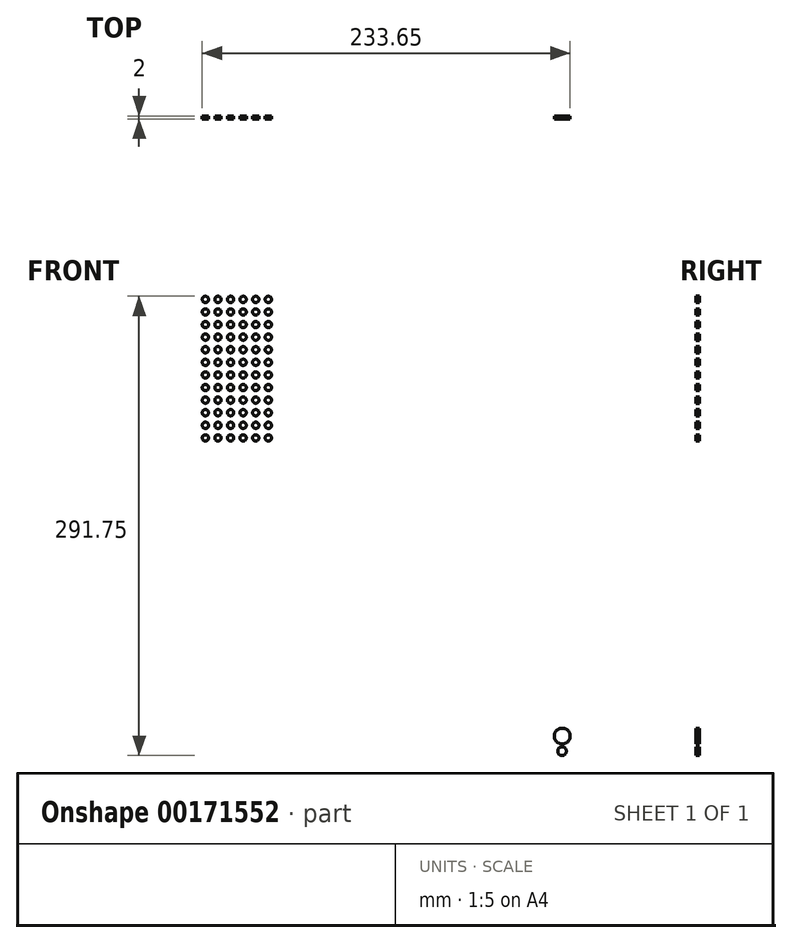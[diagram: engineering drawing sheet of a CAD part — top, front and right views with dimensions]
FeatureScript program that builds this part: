
annotation { "Feature Type Name" : "Feature", "Feature Type Description" : "" }
export const myFeature = defineFeature(function(context is Context, id is Id, definition is map)
    precondition{}
    {
        {
            var Q0;
            Q0=qCreatedBy(makeId("Front.planeOp"),FACE);
            var sketch = newSketch(context, id + "F0", { "sketchPlane" : qUnion([Q0])});
            skPoint(sketch, "E0.middle", {"position": v(0, 0) * mm});
            skLineSegment(sketch, "E1.bottom", {"start": v(127.48, 155) * mm, "end": v(157.77, 155) * mm});
            skLineSegment(sketch, "E1.top", {"start": v(127.48, -155) * mm, "end": v(158.23, -155) * mm});
            skLineSegment(sketch, "E1.right", {"start": v(157.77, 155) * mm, "end": v(158.23, -155) * mm});
            skLineSegment(sketch, "E2.bottom", {"start": v(-127.94, 155) * mm, "end": v(-158.23, 155) * mm});
            skLineSegment(sketch, "E2.top", {"start": v(-127.02, -155) * mm, "end": v(-157.77, -155) * mm});
            skLineSegment(sketch, "E2.right", {"start": v(-158.23, 155) * mm, "end": v(-157.77, -155) * mm});
            skLineSegment(sketch, "E3.top", {"start": v(-125.23, 188.22) * mm, "end": v(124.77, 188.22) * mm});
            skLineSegment(sketch, "E3.left", {"start": v(-125.23, 157.7) * mm, "end": v(-125.23, 188.22) * mm});
            skLineSegment(sketch, "E3.right", {"start": v(124.77, 157.7) * mm, "end": v(124.77, 188.22) * mm});
            skLineSegment(sketch, "E4.top", {"start": v(-124.77, -187.78) * mm, "end": v(124.77, -187.78) * mm});
            skLineSegment(sketch, "E4.left", {"start": v(-124.77, -157.26) * mm, "end": v(-124.77, -187.78) * mm});
            skLineSegment(sketch, "E4.right", {"start": v(124.77, -157.26) * mm, "end": v(124.77, -187.78) * mm});
            skLineSegment(sketch, "E5.bottom", {"start": v(-122.53, 157.7) * mm, "end": v(-125.23, 157.7) * mm});
            skLineSegment(sketch, "E5.top", {"start": v(-122.53, 152.3) * mm, "end": v(-127.94, 152.3) * mm});
            skLineSegment(sketch, "E5.left", {"start": v(-122.53, 157.7) * mm, "end": v(-122.53, 152.3) * mm});
            skLineSegment(sketch, "E5.right", {"start": v(-127.94, 155) * mm, "end": v(-127.94, 152.3) * mm});
            skPoint(sketch, "E5.middle", {"position": v(-125.23, 155) * mm});
            skLineSegment(sketch, "E6.bottom", {"start": v(124.77, 157.7) * mm, "end": v(122.06, 157.7) * mm});
            skLineSegment(sketch, "E6.top", {"start": v(127.48, 152.32) * mm, "end": v(122.06, 152.32) * mm});
            skLineSegment(sketch, "E6.left", {"start": v(127.48, 155) * mm, "end": v(127.48, 152.32) * mm});
            skLineSegment(sketch, "E6.right", {"start": v(122.06, 157.7) * mm, "end": v(122.06, 152.32) * mm});
            skPoint(sketch, "E6.middle", {"position": v(124.77, 155) * mm});
            skLineSegment(sketch, "E7.bottom", {"start": v(127.48, -152.73) * mm, "end": v(122.98, -152.73) * mm});
            skLineSegment(sketch, "E7.top", {"start": v(124.77, -157.26) * mm, "end": v(122.98, -157.26) * mm});
            skLineSegment(sketch, "E7.left", {"start": v(127.48, -152.73) * mm, "end": v(127.48, -155) * mm});
            skLineSegment(sketch, "E7.right", {"start": v(122.98, -152.73) * mm, "end": v(122.98, -157.26) * mm});
            skPoint(sketch, "E7.middle", {"position": v(125.23, -155) * mm});
            skLineSegment(sketch, "E8.bottom", {"start": v(-122.52, -152.76) * mm, "end": v(-127.02, -152.76) * mm});
            skLineSegment(sketch, "E8.top", {"start": v(-122.52, -157.26) * mm, "end": v(-124.77, -157.26) * mm});
            skLineSegment(sketch, "E8.left", {"start": v(-122.52, -152.76) * mm, "end": v(-122.52, -157.26) * mm});
            skLineSegment(sketch, "E8.right", {"start": v(-127.02, -152.76) * mm, "end": v(-127.02, -155) * mm});
            skPoint(sketch, "E8.middle", {"position": v(-124.77, -155) * mm});
            skPoint(sketch, "E9.orphan", {"position": v(127.48, 157.7) * mm});
            skPoint(sketch, "E10.orphan", {"position": v(127.48, -157.26) * mm});
            skPoint(sketch, "E11.orphan", {"position": v(-127.02, -157.26) * mm});
            skLineSegment(sketch, "E12", {"start": v(-133.23, 167.46) * mm, "end": v(-132.73, -167.53) * mm, "construction": true});
            skLineSegment(sketch, "E13.bottom", {"start": v(55, 130.25) * mm, "end": v(-55, 130.25) * mm});
            skLineSegment(sketch, "E13.top", {"start": v(55, 59.75) * mm, "end": v(-55, 59.75) * mm});
            skLineSegment(sketch, "E13.left", {"start": v(55, 130.25) * mm, "end": v(55, 59.75) * mm});
            skLineSegment(sketch, "E13.right", {"start": v(-55, 130.25) * mm, "end": v(-55, 59.75) * mm});
            skPoint(sketch, "E13.middle", {"position": v(0, 95) * mm});
            skLineSegment(sketch, "E14.bottom", {"start": v(59, 134.5) * mm, "end": v(-59, 134.5) * mm, "construction": true});
            skLineSegment(sketch, "E14.top", {"start": v(59, 55.5) * mm, "end": v(-59, 55.5) * mm, "construction": true});
            skLineSegment(sketch, "E14.left", {"start": v(59, 134.5) * mm, "end": v(59, 55.5) * mm, "construction": true});
            skLineSegment(sketch, "E14.right", {"start": v(-59, 134.5) * mm, "end": v(-59, 55.5) * mm, "construction": true});
            skCircle(sketch, "E15", {"center": v(-59, 134.5) * mm, "radius": 2.75 * mm});
            skCircle(sketch, "E16", {"center": v(-59, 55.5) * mm, "radius": 2.75 * mm});
            skCircle(sketch, "E17", {"center": v(59, 55.5) * mm, "radius": 2.75 * mm});
            skCircle(sketch, "E18", {"center": v(59, 134.5) * mm, "radius": 2.75 * mm});
            skLineSegment(sketch, "E19.bottom", {"start": v(65, 140.5) * mm, "end": v(-65, 140.5) * mm, "construction": true});
            skLineSegment(sketch, "E19.top", {"start": v(65, 49.5) * mm, "end": v(-65, 49.5) * mm, "construction": true});
            skLineSegment(sketch, "E19.left", {"start": v(65, 140.5) * mm, "end": v(65, 49.5) * mm, "construction": true});
            skLineSegment(sketch, "E19.right", {"start": v(-65, 140.5) * mm, "end": v(-65, 49.5) * mm, "construction": true});
            skCircle(sketch, "E20", {"center": v(-150.33, -112.4) * mm, "radius": 4 * mm});
            skCircle(sketch, "E21", {"center": v(-150.33, 34.3) * mm, "radius": 4.5 * mm});
            skCircle(sketch, "E22", {"center": v(-150.33, 149.07) * mm, "radius": 4.5 * mm});
            skCircle(sketch, "E23", {"center": v(-150.33, 72.92) * mm, "radius": 4.5 * mm});
            skCircle(sketch, "E24.MirrorC", {"center": v(150.33, 149.07) * mm, "radius": 4.5 * mm});
            skCircle(sketch, "E25.MirrorC", {"center": v(150.33, 72.92) * mm, "radius": 4.5 * mm});
            skCircle(sketch, "E26.MirrorC", {"center": v(150.33, 34.3) * mm, "radius": 4.5 * mm});
            skCircle(sketch, "E27.MirrorC", {"center": v(150.33, -112.4) * mm, "radius": 4 * mm});
            skCircle(sketch, "E28", {"center": v(0, -175.28) * mm, "radius": 4 * mm});
            skCircle(sketch, "E29", {"center": v(-95, -175.28) * mm, "radius": 4 * mm});
            skCircle(sketch, "E30", {"center": v(95, -175.28) * mm, "radius": 4 * mm});
            skCircle(sketch, "E31.MirrorC", {"center": v(-95, 175.28) * mm, "radius": 4 * mm});
            skCircle(sketch, "E32.MirrorC", {"center": v(95, 175.28) * mm, "radius": 4 * mm});
            skCircle(sketch, "E33.MirrorC", {"center": v(0, 175.28) * mm, "radius": 4 * mm});
            skSolve(sketch);
        }
        {
            var Q0;
            Q0=makeQuery(id+"F0.imprint","IMPRINT",FACE,{"disambiguationData":[TD([[makeQuery(id+"F0.imprint","IMPRINT",EDGE,{"derivedFrom":sQuery(id+"F0.wireOp",EDGE,"E1.bottom")}),-1.0]])]});
            extrude(context, id + "F1", {"entities" : qUnion([Q0]), "endBound" : BoundingType.SYMMETRIC, "depth" : 2 * mm});
        }
        {
            var Q0;
            Q0=makeQuery(id+"F1.opExtrude","SWEPT_EDGE",EDGE,{"disambiguationData":[OSD([sQuery(id+"F0.wireOp",EDGE,"E1.bottom"),sQuery(id+"F0.wireOp",EDGE,"E1.right")])]});
            var Q1;
            Q1=makeQuery(id+"F1.opExtrude","SWEPT_EDGE",EDGE,{"disambiguationData":[OSD([sQuery(id+"F0.wireOp",EDGE,"E3.top"),sQuery(id+"F0.wireOp",EDGE,"E3.right")])]});
            var Q2;
            Q2=makeQuery(id+"F1.opExtrude","SWEPT_EDGE",EDGE,{"disambiguationData":[OSD([sQuery(id+"F0.wireOp",EDGE,"E3.top"),sQuery(id+"F0.wireOp",EDGE,"E3.left")])]});
            var Q3;
            Q3=makeQuery(id+"F1.opExtrude","SWEPT_EDGE",EDGE,{"disambiguationData":[OSD([sQuery(id+"F0.wireOp",EDGE,"E2.bottom"),sQuery(id+"F0.wireOp",EDGE,"E2.right")])]});
            var Q4;
            Q4=makeQuery(id+"F1.opExtrude","SWEPT_EDGE",EDGE,{"disambiguationData":[OSD([sQuery(id+"F0.wireOp",EDGE,"E1.top"),sQuery(id+"F0.wireOp",EDGE,"E1.right")])]});
            var Q5;
            Q5=makeQuery(id+"F1.opExtrude","SWEPT_EDGE",EDGE,{"disambiguationData":[OSD([sQuery(id+"F0.wireOp",EDGE,"E4.top"),sQuery(id+"F0.wireOp",EDGE,"E4.right")])]});
            var Q6;
            Q6=makeQuery(id+"F1.opExtrude","SWEPT_EDGE",EDGE,{"disambiguationData":[OSD([sQuery(id+"F0.wireOp",EDGE,"E4.top"),sQuery(id+"F0.wireOp",EDGE,"E4.left")])]});
            var Q7;
            Q7=makeQuery(id+"F1.opExtrude","SWEPT_EDGE",EDGE,{"disambiguationData":[OSD([sQuery(id+"F0.wireOp",EDGE,"E2.top"),sQuery(id+"F0.wireOp",EDGE,"E2.right")])]});
            chamfer(context, id + "F2", {"entities" : qUnion([Q0, Q1, Q2, Q3, Q4, Q5, Q6, Q7]), "width" : 6 * mm, "tangentPropagation" : true});
        }
        {
            var Q0;
            Q0=makeQuery(id+"F1.opExtrude","CAP_FACE",FACE,{"disambiguationData":[OSD([sQuery(id+"F0.wireOp",EDGE,"E1.bottom"),sQuery(id+"F0.wireOp",EDGE,"E1.top"),sQuery(id+"F0.wireOp",EDGE,"E1.right"),sQuery(id+"F0.wireOp",EDGE,"E2.bottom"),sQuery(id+"F0.wireOp",EDGE,"E2.top"),sQuery(id+"F0.wireOp",EDGE,"E2.right"),sQuery(id+"F0.wireOp",EDGE,"E3.top"),sQuery(id+"F0.wireOp",EDGE,"E3.left"),sQuery(id+"F0.wireOp",EDGE,"E3.right"),sQuery(id+"F0.wireOp",EDGE,"E4.top"),sQuery(id+"F0.wireOp",EDGE,"E4.left"),sQuery(id+"F0.wireOp",EDGE,"E4.right"),sQuery(id+"F0.wireOp",EDGE,"E5.bottom"),sQuery(id+"F0.wireOp",EDGE,"E5.top"),sQuery(id+"F0.wireOp",EDGE,"E5.left"),sQuery(id+"F0.wireOp",EDGE,"E5.right"),sQuery(id+"F0.wireOp",EDGE,"E6.bottom"),sQuery(id+"F0.wireOp",EDGE,"E6.top"),sQuery(id+"F0.wireOp",EDGE,"E6.left"),sQuery(id+"F0.wireOp",EDGE,"E6.right"),sQuery(id+"F0.wireOp",EDGE,"E7.bottom"),sQuery(id+"F0.wireOp",EDGE,"E7.top"),sQuery(id+"F0.wireOp",EDGE,"E7.left"),sQuery(id+"F0.wireOp",EDGE,"E7.right"),sQuery(id+"F0.wireOp",EDGE,"E8.bottom"),sQuery(id+"F0.wireOp",EDGE,"E8.top"),sQuery(id+"F0.wireOp",EDGE,"E8.left"),sQuery(id+"F0.wireOp",EDGE,"E8.right"),sQuery(id+"F0.wireOp",EDGE,"E13.bottom"),sQuery(id+"F0.wireOp",EDGE,"E13.top"),sQuery(id+"F0.wireOp",EDGE,"E13.left"),sQuery(id+"F0.wireOp",EDGE,"E13.right"),sQuery(id+"F0.wireOp",EDGE,"E15"),sQuery(id+"F0.wireOp",EDGE,"E16"),sQuery(id+"F0.wireOp",EDGE,"E17"),sQuery(id+"F0.wireOp",EDGE,"E18")])],"isStart":false});
            var sketch = newSketch(context, id + "F3", { "sketchPlane" : qUnion([Q0])});
            skCircle(sketch, "E34", {"center": v(109.77, -140) * mm, "radius": 2.75 * mm});
            skLineSegment(sketch, "E35", {"start": v(106.88, -130.39) * mm, "end": v(112.88, -130.39) * mm});
            skLineSegment(sketch, "E36", {"start": v(107.88, -131.39) * mm, "end": v(111.88, -131.39) * mm});
            skLineSegment(sketch, "E37", {"start": v(108.88, -132.39) * mm, "end": v(110.88, -132.39) * mm});
            skLineSegment(sketch, "E38", {"start": v(109.88, -130.39) * mm, "end": v(109.88, -126.39) * mm});
            skCircle(sketch, "E39", {"center": v(109.88, -130.39) * mm, "radius": 5 * mm});
            skSolve(sketch);
        }
        {
            var Q0;
            Q0=makeQuery(id+"F3.imprint","IMPRINT",FACE,{"disambiguationData":[TD([[makeQuery(id+"F3.imprint","IMPRINT",EDGE,{"derivedFrom":sQuery(id+"F3.wireOp",EDGE,"E34")}),-1.0]])]});
            var sketch = newSketch(context, id + "F4", { "sketchPlane" : qUnion([Q0])});
            skCircle(sketch, "E40", {"center": v(116.77, 147) * mm, "radius": 2 * mm});
            skCircle(sketch, "E41.0.1.0", {"center": v(116.77, 139) * mm, "radius": 2 * mm});
            skCircle(sketch, "E41.0.2.0", {"center": v(116.77, 131) * mm, "radius": 2 * mm});
            skCircle(sketch, "E41.0.3.0", {"center": v(116.77, 123) * mm, "radius": 2 * mm});
            skCircle(sketch, "E41.0.4.0", {"center": v(116.77, 115) * mm, "radius": 2 * mm});
            skCircle(sketch, "E41.0.5.0", {"center": v(116.77, 107) * mm, "radius": 2 * mm});
            skCircle(sketch, "E41.0.6.0", {"center": v(116.77, 99) * mm, "radius": 2 * mm});
            skCircle(sketch, "E41.0.7.0", {"center": v(116.77, 91) * mm, "radius": 2 * mm});
            skCircle(sketch, "E41.0.8.0", {"center": v(116.77, 83) * mm, "radius": 2 * mm});
            skCircle(sketch, "E41.0.9.0", {"center": v(116.77, 75) * mm, "radius": 2 * mm});
            skCircle(sketch, "E41.0.10.0", {"center": v(116.77, 67) * mm, "radius": 2 * mm});
            skCircle(sketch, "E41.0.11.0", {"center": v(116.77, 59) * mm, "radius": 2 * mm});
            skCircle(sketch, "E41.1.0.0", {"center": v(108.77, 147) * mm, "radius": 2 * mm});
            skCircle(sketch, "E41.1.1.0", {"center": v(108.77, 139) * mm, "radius": 2 * mm});
            skCircle(sketch, "E41.1.2.0", {"center": v(108.77, 131) * mm, "radius": 2 * mm});
            skCircle(sketch, "E41.1.3.0", {"center": v(108.77, 123) * mm, "radius": 2 * mm});
            skCircle(sketch, "E41.1.4.0", {"center": v(108.77, 115) * mm, "radius": 2 * mm});
            skCircle(sketch, "E41.1.5.0", {"center": v(108.77, 107) * mm, "radius": 2 * mm});
            skCircle(sketch, "E41.1.6.0", {"center": v(108.77, 99) * mm, "radius": 2 * mm});
            skCircle(sketch, "E41.1.7.0", {"center": v(108.77, 91) * mm, "radius": 2 * mm});
            skCircle(sketch, "E41.1.8.0", {"center": v(108.77, 83) * mm, "radius": 2 * mm});
            skCircle(sketch, "E41.1.9.0", {"center": v(108.77, 75) * mm, "radius": 2 * mm});
            skCircle(sketch, "E41.1.10.0", {"center": v(108.77, 67) * mm, "radius": 2 * mm});
            skCircle(sketch, "E41.1.11.0", {"center": v(108.77, 59) * mm, "radius": 2 * mm});
            skCircle(sketch, "E41.2.0.0", {"center": v(100.77, 147) * mm, "radius": 2 * mm});
            skCircle(sketch, "E41.2.1.0", {"center": v(100.77, 139) * mm, "radius": 2 * mm});
            skCircle(sketch, "E41.2.2.0", {"center": v(100.77, 131) * mm, "radius": 2 * mm});
            skCircle(sketch, "E41.2.3.0", {"center": v(100.77, 123) * mm, "radius": 2 * mm});
            skCircle(sketch, "E41.2.4.0", {"center": v(100.77, 115) * mm, "radius": 2 * mm});
            skCircle(sketch, "E41.2.5.0", {"center": v(100.77, 107) * mm, "radius": 2 * mm});
            skCircle(sketch, "E41.2.6.0", {"center": v(100.77, 99) * mm, "radius": 2 * mm});
            skCircle(sketch, "E41.2.7.0", {"center": v(100.77, 91) * mm, "radius": 2 * mm});
            skCircle(sketch, "E41.2.8.0", {"center": v(100.77, 83) * mm, "radius": 2 * mm});
            skCircle(sketch, "E41.2.9.0", {"center": v(100.77, 75) * mm, "radius": 2 * mm});
            skCircle(sketch, "E41.2.10.0", {"center": v(100.77, 67) * mm, "radius": 2 * mm});
            skCircle(sketch, "E41.2.11.0", {"center": v(100.77, 59) * mm, "radius": 2 * mm});
            skCircle(sketch, "E41.3.0.0", {"center": v(92.77, 147) * mm, "radius": 2 * mm});
            skCircle(sketch, "E41.3.1.0", {"center": v(92.77, 139) * mm, "radius": 2 * mm});
            skCircle(sketch, "E41.3.2.0", {"center": v(92.77, 131) * mm, "radius": 2 * mm});
            skCircle(sketch, "E41.3.3.0", {"center": v(92.77, 123) * mm, "radius": 2 * mm});
            skCircle(sketch, "E41.3.4.0", {"center": v(92.77, 115) * mm, "radius": 2 * mm});
            skCircle(sketch, "E41.3.5.0", {"center": v(92.77, 107) * mm, "radius": 2 * mm});
            skCircle(sketch, "E41.3.6.0", {"center": v(92.77, 99) * mm, "radius": 2 * mm});
            skCircle(sketch, "E41.3.7.0", {"center": v(92.77, 91) * mm, "radius": 2 * mm});
            skCircle(sketch, "E41.3.8.0", {"center": v(92.77, 83) * mm, "radius": 2 * mm});
            skCircle(sketch, "E41.3.9.0", {"center": v(92.77, 75) * mm, "radius": 2 * mm});
            skCircle(sketch, "E41.3.10.0", {"center": v(92.77, 67) * mm, "radius": 2 * mm});
            skCircle(sketch, "E41.3.11.0", {"center": v(92.77, 59) * mm, "radius": 2 * mm});
            skCircle(sketch, "E41.4.0.0", {"center": v(84.77, 147) * mm, "radius": 2 * mm});
            skCircle(sketch, "E41.4.1.0", {"center": v(84.77, 139) * mm, "radius": 2 * mm});
            skCircle(sketch, "E41.4.2.0", {"center": v(84.77, 131) * mm, "radius": 2 * mm});
            skCircle(sketch, "E41.4.3.0", {"center": v(84.77, 123) * mm, "radius": 2 * mm});
            skCircle(sketch, "E41.4.4.0", {"center": v(84.77, 115) * mm, "radius": 2 * mm});
            skCircle(sketch, "E41.4.5.0", {"center": v(84.77, 107) * mm, "radius": 2 * mm});
            skCircle(sketch, "E41.4.6.0", {"center": v(84.77, 99) * mm, "radius": 2 * mm});
            skCircle(sketch, "E41.4.7.0", {"center": v(84.77, 91) * mm, "radius": 2 * mm});
            skCircle(sketch, "E41.4.8.0", {"center": v(84.77, 83) * mm, "radius": 2 * mm});
            skCircle(sketch, "E41.4.9.0", {"center": v(84.77, 75) * mm, "radius": 2 * mm});
            skCircle(sketch, "E41.4.10.0", {"center": v(84.77, 67) * mm, "radius": 2 * mm});
            skCircle(sketch, "E41.4.11.0", {"center": v(84.77, 59) * mm, "radius": 2 * mm});
            skCircle(sketch, "E41.5.0.0", {"center": v(76.77, 147) * mm, "radius": 2 * mm});
            skCircle(sketch, "E41.5.1.0", {"center": v(76.77, 139) * mm, "radius": 2 * mm});
            skCircle(sketch, "E41.5.2.0", {"center": v(76.77, 131) * mm, "radius": 2 * mm});
            skCircle(sketch, "E41.5.3.0", {"center": v(76.77, 123) * mm, "radius": 2 * mm});
            skCircle(sketch, "E41.5.4.0", {"center": v(76.77, 115) * mm, "radius": 2 * mm});
            skCircle(sketch, "E41.5.5.0", {"center": v(76.77, 107) * mm, "radius": 2 * mm});
            skCircle(sketch, "E41.5.6.0", {"center": v(76.77, 99) * mm, "radius": 2 * mm});
            skCircle(sketch, "E41.5.7.0", {"center": v(76.77, 91) * mm, "radius": 2 * mm});
            skCircle(sketch, "E41.5.8.0", {"center": v(76.77, 83) * mm, "radius": 2 * mm});
            skCircle(sketch, "E41.5.9.0", {"center": v(76.77, 75) * mm, "radius": 2 * mm});
            skCircle(sketch, "E41.5.10.0", {"center": v(76.77, 67) * mm, "radius": 2 * mm});
            skCircle(sketch, "E41.5.11.0", {"center": v(76.77, 59) * mm, "radius": 2 * mm});
            skLineSegment(sketch, "E41.direction1", {"start": v(116.77, 147) * mm, "end": v(108.77, 147) * mm, "construction": true});
            skLineSegment(sketch, "E41.direction2", {"start": v(116.77, 147) * mm, "end": v(116.77, 139) * mm, "construction": true});
            skCircle(sketch, "E42.MirrorC", {"center": v(-116.77, 147) * mm, "radius": 2 * mm});
            skCircle(sketch, "E43.MirrorC", {"center": v(-108.77, 147) * mm, "radius": 2 * mm});
            skCircle(sketch, "E44.MirrorC", {"center": v(-116.77, 139) * mm, "radius": 2 * mm});
            skCircle(sketch, "E45.MirrorC", {"center": v(-76.77, 75) * mm, "radius": 2 * mm});
            skCircle(sketch, "E46.MirrorC", {"center": v(-76.77, 131) * mm, "radius": 2 * mm});
            skCircle(sketch, "E47.MirrorC", {"center": v(-108.77, 75) * mm, "radius": 2 * mm});
            skCircle(sketch, "E48.MirrorC", {"center": v(-92.77, 139) * mm, "radius": 2 * mm});
            skCircle(sketch, "E49.MirrorC", {"center": v(-100.77, 99) * mm, "radius": 2 * mm});
            skCircle(sketch, "E50.MirrorC", {"center": v(-92.77, 67) * mm, "radius": 2 * mm});
            skCircle(sketch, "E51.MirrorC", {"center": v(-84.77, 107) * mm, "radius": 2 * mm});
            skCircle(sketch, "E52.MirrorC", {"center": v(-92.77, 83) * mm, "radius": 2 * mm});
            skCircle(sketch, "E53.MirrorC", {"center": v(-76.77, 147) * mm, "radius": 2 * mm});
            skCircle(sketch, "E54.MirrorC", {"center": v(-100.77, 115) * mm, "radius": 2 * mm});
            skCircle(sketch, "E55.MirrorC", {"center": v(-76.77, 83) * mm, "radius": 2 * mm});
            skCircle(sketch, "E56.MirrorC", {"center": v(-76.77, 139) * mm, "radius": 2 * mm});
            skCircle(sketch, "E57.MirrorC", {"center": v(-116.77, 59) * mm, "radius": 2 * mm});
            skCircle(sketch, "E58.MirrorC", {"center": v(-108.77, 83) * mm, "radius": 2 * mm});
            skCircle(sketch, "E59.MirrorC", {"center": v(-92.77, 147) * mm, "radius": 2 * mm});
            skCircle(sketch, "E60.MirrorC", {"center": v(-100.77, 107) * mm, "radius": 2 * mm});
            skCircle(sketch, "E61.MirrorC", {"center": v(-92.77, 75) * mm, "radius": 2 * mm});
            skCircle(sketch, "E62.MirrorC", {"center": v(-84.77, 115) * mm, "radius": 2 * mm});
            skCircle(sketch, "E63.MirrorC", {"center": v(-116.77, 67) * mm, "radius": 2 * mm});
            skCircle(sketch, "E64.MirrorC", {"center": v(-116.77, 75) * mm, "radius": 2 * mm});
            skCircle(sketch, "E65.MirrorC", {"center": v(-116.77, 83) * mm, "radius": 2 * mm});
            skCircle(sketch, "E66.MirrorC", {"center": v(-116.77, 91) * mm, "radius": 2 * mm});
            skCircle(sketch, "E67.MirrorC", {"center": v(-116.77, 99) * mm, "radius": 2 * mm});
            skCircle(sketch, "E68.MirrorC", {"center": v(-116.77, 107) * mm, "radius": 2 * mm});
            skCircle(sketch, "E69.MirrorC", {"center": v(-92.77, 91) * mm, "radius": 2 * mm});
            skCircle(sketch, "E70.MirrorC", {"center": v(-84.77, 59) * mm, "radius": 2 * mm});
            skCircle(sketch, "E71.MirrorC", {"center": v(-116.77, 115) * mm, "radius": 2 * mm});
            skCircle(sketch, "E72.MirrorC", {"center": v(-116.77, 123) * mm, "radius": 2 * mm});
            skCircle(sketch, "E73.MirrorC", {"center": v(-100.77, 123) * mm, "radius": 2 * mm});
            skCircle(sketch, "E74.MirrorC", {"center": v(-116.77, 131) * mm, "radius": 2 * mm});
            skCircle(sketch, "E75.MirrorC", {"center": v(-108.77, 123) * mm, "radius": 2 * mm});
            skCircle(sketch, "E76.MirrorC", {"center": v(-108.77, 131) * mm, "radius": 2 * mm});
            skCircle(sketch, "E77.MirrorC", {"center": v(-108.77, 139) * mm, "radius": 2 * mm});
            skCircle(sketch, "E78.MirrorC", {"center": v(-76.77, 91) * mm, "radius": 2 * mm});
            skCircle(sketch, "E79.MirrorC", {"center": v(-108.77, 91) * mm, "radius": 2 * mm});
            skCircle(sketch, "E80.MirrorC", {"center": v(-100.77, 59) * mm, "radius": 2 * mm});
            skCircle(sketch, "E81.MirrorC", {"center": v(-84.77, 123) * mm, "radius": 2 * mm});
            skCircle(sketch, "E82.MirrorC", {"center": v(-92.77, 99) * mm, "radius": 2 * mm});
            skCircle(sketch, "E83.MirrorC", {"center": v(-84.77, 67) * mm, "radius": 2 * mm});
            skCircle(sketch, "E84.MirrorC", {"center": v(-100.77, 131) * mm, "radius": 2 * mm});
            skCircle(sketch, "E85.MirrorC", {"center": v(-76.77, 99) * mm, "radius": 2 * mm});
            skCircle(sketch, "E86.MirrorC", {"center": v(-108.77, 99) * mm, "radius": 2 * mm});
            skCircle(sketch, "E87.MirrorC", {"center": v(-100.77, 67) * mm, "radius": 2 * mm});
            skCircle(sketch, "E88.MirrorC", {"center": v(-84.77, 131) * mm, "radius": 2 * mm});
            skCircle(sketch, "E89.MirrorC", {"center": v(-92.77, 107) * mm, "radius": 2 * mm});
            skCircle(sketch, "E90.MirrorC", {"center": v(-84.77, 75) * mm, "radius": 2 * mm});
            skLineSegment(sketch, "E91.MirrorCS", {"start": v(-116.77, 147) * mm, "end": v(-116.77, 139) * mm, "construction": true});
            skCircle(sketch, "E92.MirrorC", {"center": v(-100.77, 139) * mm, "radius": 2 * mm});
            skCircle(sketch, "E93.MirrorC", {"center": v(-108.77, 107) * mm, "radius": 2 * mm});
            skCircle(sketch, "E94.MirrorC", {"center": v(-100.77, 75) * mm, "radius": 2 * mm});
            skCircle(sketch, "E95.MirrorC", {"center": v(-84.77, 139) * mm, "radius": 2 * mm});
            skCircle(sketch, "E96.MirrorC", {"center": v(-92.77, 115) * mm, "radius": 2 * mm});
            skCircle(sketch, "E97.MirrorC", {"center": v(-84.77, 83) * mm, "radius": 2 * mm});
            skCircle(sketch, "E98.MirrorC", {"center": v(-100.77, 147) * mm, "radius": 2 * mm});
            skCircle(sketch, "E99.MirrorC", {"center": v(-76.77, 107) * mm, "radius": 2 * mm});
            skCircle(sketch, "E100.MirrorC", {"center": v(-92.77, 123) * mm, "radius": 2 * mm});
            skCircle(sketch, "E101.MirrorC", {"center": v(-84.77, 91) * mm, "radius": 2 * mm});
            skCircle(sketch, "E102.MirrorC", {"center": v(-76.77, 59) * mm, "radius": 2 * mm});
            skCircle(sketch, "E103.MirrorC", {"center": v(-108.77, 59) * mm, "radius": 2 * mm});
            skCircle(sketch, "E104.MirrorC", {"center": v(-76.77, 115) * mm, "radius": 2 * mm});
            skCircle(sketch, "E105.MirrorC", {"center": v(-108.77, 115) * mm, "radius": 2 * mm});
            skCircle(sketch, "E106.MirrorC", {"center": v(-100.77, 83) * mm, "radius": 2 * mm});
            skCircle(sketch, "E107.MirrorC", {"center": v(-84.77, 147) * mm, "radius": 2 * mm});
            skCircle(sketch, "E108.MirrorC", {"center": v(-76.77, 123) * mm, "radius": 2 * mm});
            skCircle(sketch, "E109.MirrorC", {"center": v(-76.77, 67) * mm, "radius": 2 * mm});
            skCircle(sketch, "E110.MirrorC", {"center": v(-108.77, 67) * mm, "radius": 2 * mm});
            skCircle(sketch, "E111.MirrorC", {"center": v(-92.77, 131) * mm, "radius": 2 * mm});
            skCircle(sketch, "E112.MirrorC", {"center": v(-100.77, 91) * mm, "radius": 2 * mm});
            skCircle(sketch, "E113.MirrorC", {"center": v(-84.77, 99) * mm, "radius": 2 * mm});
            skCircle(sketch, "E114.MirrorC", {"center": v(-92.77, 59) * mm, "radius": 2 * mm});
            skLineSegment(sketch, "E115.MirrorCS", {"start": v(-116.77, 147) * mm, "end": v(-108.77, 147) * mm, "construction": true});
            skSolve(sketch);
        }
        {
            var Q0;
            Q0=makeQuery(id+"F4.imprint","IMPRINT",FACE,{"disambiguationData":[TD([[makeQuery(id+"F4.imprint","IMPRINT",EDGE,{"derivedFrom":sQuery(id+"F4.wireOp",EDGE,"E103.MirrorC")}),-1.0]])]});
            var Q1;
            Q1=makeQuery(id+"F4.imprint","IMPRINT",FACE,{"disambiguationData":[TD([[makeQuery(id+"F4.imprint","IMPRINT",EDGE,{"derivedFrom":sQuery(id+"F4.wireOp",EDGE,"E106.MirrorC")}),-1.0]])]});
            var Q2;
            Q2=makeQuery(id+"F4.imprint","IMPRINT",FACE,{"disambiguationData":[TD([[makeQuery(id+"F4.imprint","IMPRINT",EDGE,{"derivedFrom":sQuery(id+"F4.wireOp",EDGE,"E89.MirrorC")}),-1.0]])]});
            var Q3;
            Q3=makeQuery(id+"F4.imprint","IMPRINT",FACE,{"disambiguationData":[TD([[makeQuery(id+"F4.imprint","IMPRINT",EDGE,{"derivedFrom":sQuery(id+"F4.wireOp",EDGE,"E57.MirrorC")}),-1.0]])]});
            var Q4;
            Q4=makeQuery(id+"F4.imprint","IMPRINT",FACE,{"disambiguationData":[TD([[makeQuery(id+"F4.imprint","IMPRINT",EDGE,{"derivedFrom":sQuery(id+"F4.wireOp",EDGE,"E54.MirrorC")}),-1.0]])]});
            var Q5;
            Q5=makeQuery(id+"F4.imprint","IMPRINT",FACE,{"disambiguationData":[TD([[makeQuery(id+"F4.imprint","IMPRINT",EDGE,{"derivedFrom":sQuery(id+"F4.wireOp",EDGE,"E70.MirrorC")}),-1.0]])]});
            var Q6;
            Q6=makeQuery(id+"F4.imprint","IMPRINT",FACE,{"disambiguationData":[TD([[makeQuery(id+"F4.imprint","IMPRINT",EDGE,{"derivedFrom":sQuery(id+"F4.wireOp",EDGE,"E72.MirrorC")}),-1.0]])]});
            var Q7;
            Q7=makeQuery(id+"F4.imprint","IMPRINT",FACE,{"disambiguationData":[TD([[makeQuery(id+"F4.imprint","IMPRINT",EDGE,{"derivedFrom":sQuery(id+"F4.wireOp",EDGE,"E86.MirrorC")}),-1.0]])]});
            var Q8;
            Q8=makeQuery(id+"F4.imprint","IMPRINT",FACE,{"disambiguationData":[TD([[makeQuery(id+"F4.imprint","IMPRINT",EDGE,{"derivedFrom":sQuery(id+"F4.wireOp",EDGE,"E88.MirrorC")}),-1.0]])]});
            var Q9;
            Q9=makeQuery(id+"F4.imprint","IMPRINT",FACE,{"disambiguationData":[TD([[makeQuery(id+"F4.imprint","IMPRINT",EDGE,{"derivedFrom":sQuery(id+"F4.wireOp",EDGE,"E105.MirrorC")}),-1.0]])]});
            var Q10;
            Q10=makeQuery(id+"F4.imprint","IMPRINT",FACE,{"disambiguationData":[TD([[makeQuery(id+"F4.imprint","IMPRINT",EDGE,{"derivedFrom":sQuery(id+"F4.wireOp",EDGE,"E56.MirrorC")}),-1.0]])]});
            var Q11;
            Q11=makeQuery(id+"F4.imprint","IMPRINT",FACE,{"disambiguationData":[TD([[makeQuery(id+"F4.imprint","IMPRINT",EDGE,{"derivedFrom":sQuery(id+"F4.wireOp",EDGE,"E102.MirrorC")}),-1.0]])]});
            var Q12;
            Q12=makeQuery(id+"F4.imprint","IMPRINT",FACE,{"disambiguationData":[TD([[makeQuery(id+"F4.imprint","IMPRINT",EDGE,{"derivedFrom":sQuery(id+"F4.wireOp",EDGE,"E53.MirrorC")}),-1.0]])]});
            var Q13;
            Q13=makeQuery(id+"F4.imprint","IMPRINT",FACE,{"disambiguationData":[TD([[makeQuery(id+"F4.imprint","IMPRINT",EDGE,{"derivedFrom":sQuery(id+"F4.wireOp",EDGE,"E69.MirrorC")}),-1.0]])]});
            var Q14;
            Q14=makeQuery(id+"F4.imprint","IMPRINT",FACE,{"disambiguationData":[TD([[makeQuery(id+"F4.imprint","IMPRINT",EDGE,{"derivedFrom":sQuery(id+"F4.wireOp",EDGE,"E85.MirrorC")}),-1.0]])]});
            var Q15;
            Q15=makeQuery(id+"F4.imprint","IMPRINT",FACE,{"disambiguationData":[TD([[makeQuery(id+"F4.imprint","IMPRINT",EDGE,{"derivedFrom":sQuery(id+"F4.wireOp",EDGE,"E101.MirrorC")}),-1.0]])]});
            var Q16;
            Q16=makeQuery(id+"F4.imprint","IMPRINT",FACE,{"disambiguationData":[TD([[makeQuery(id+"F4.imprint","IMPRINT",EDGE,{"derivedFrom":sQuery(id+"F4.wireOp",EDGE,"E104.MirrorC")}),-1.0]])]});
            var Q17;
            Q17=makeQuery(id+"F4.imprint","IMPRINT",FACE,{"disambiguationData":[TD([[makeQuery(id+"F4.imprint","IMPRINT",EDGE,{"derivedFrom":sQuery(id+"F4.wireOp",EDGE,"E52.MirrorC")}),-1.0]])]});
            var Q18;
            Q18=makeQuery(id+"F4.imprint","IMPRINT",FACE,{"disambiguationData":[TD([[makeQuery(id+"F4.imprint","IMPRINT",EDGE,{"derivedFrom":sQuery(id+"F4.wireOp",EDGE,"E68.MirrorC")}),-1.0]])]});
            var Q19;
            Q19=makeQuery(id+"F4.imprint","IMPRINT",FACE,{"disambiguationData":[TD([[makeQuery(id+"F4.imprint","IMPRINT",EDGE,{"derivedFrom":sQuery(id+"F4.wireOp",EDGE,"E84.MirrorC")}),-1.0]])]});
            var Q20;
            Q20=makeQuery(id+"F4.imprint","IMPRINT",FACE,{"disambiguationData":[TD([[makeQuery(id+"F4.imprint","IMPRINT",EDGE,{"derivedFrom":sQuery(id+"F4.wireOp",EDGE,"E100.MirrorC")}),-1.0]])]});
            var Q21;
            Q21=makeQuery(id+"F4.imprint","IMPRINT",FACE,{"disambiguationData":[TD([[makeQuery(id+"F4.imprint","IMPRINT",EDGE,{"derivedFrom":sQuery(id+"F4.wireOp",EDGE,"E51.MirrorC")}),-1.0]])]});
            var Q22;
            Q22=makeQuery(id+"F4.imprint","IMPRINT",FACE,{"disambiguationData":[TD([[makeQuery(id+"F4.imprint","IMPRINT",EDGE,{"derivedFrom":sQuery(id+"F4.wireOp",EDGE,"E55.MirrorC")}),-1.0]])]});
            var Q23;
            Q23=makeQuery(id+"F4.imprint","IMPRINT",FACE,{"disambiguationData":[TD([[makeQuery(id+"F4.imprint","IMPRINT",EDGE,{"derivedFrom":sQuery(id+"F4.wireOp",EDGE,"E67.MirrorC")}),-1.0]])]});
            var Q24;
            Q24=makeQuery(id+"F4.imprint","IMPRINT",FACE,{"disambiguationData":[TD([[makeQuery(id+"F4.imprint","IMPRINT",EDGE,{"derivedFrom":sQuery(id+"F4.wireOp",EDGE,"E83.MirrorC")}),-1.0]])]});
            var Q25;
            Q25=makeQuery(id+"F4.imprint","IMPRINT",FACE,{"disambiguationData":[TD([[makeQuery(id+"F4.imprint","IMPRINT",EDGE,{"derivedFrom":sQuery(id+"F4.wireOp",EDGE,"E71.MirrorC")}),-1.0]])]});
            var Q26;
            Q26=makeQuery(id+"F4.imprint","IMPRINT",FACE,{"disambiguationData":[TD([[makeQuery(id+"F4.imprint","IMPRINT",EDGE,{"derivedFrom":sQuery(id+"F4.wireOp",EDGE,"E99.MirrorC")}),-1.0]])]});
            var Q27;
            Q27=makeQuery(id+"F4.imprint","IMPRINT",FACE,{"disambiguationData":[TD([[makeQuery(id+"F4.imprint","IMPRINT",EDGE,{"derivedFrom":sQuery(id+"F4.wireOp",EDGE,"E87.MirrorC")}),-1.0]])]});
            var Q28;
            Q28=makeQuery(id+"F4.imprint","IMPRINT",FACE,{"disambiguationData":[TD([[makeQuery(id+"F4.imprint","IMPRINT",EDGE,{"derivedFrom":sQuery(id+"F4.wireOp",EDGE,"E50.MirrorC")}),-1.0]])]});
            var Q29;
            Q29=makeQuery(id+"F4.imprint","IMPRINT",FACE,{"disambiguationData":[TD([[makeQuery(id+"F4.imprint","IMPRINT",EDGE,{"derivedFrom":sQuery(id+"F4.wireOp",EDGE,"E82.MirrorC")}),-1.0]])]});
            var Q30;
            Q30=makeQuery(id+"F4.imprint","IMPRINT",FACE,{"disambiguationData":[TD([[makeQuery(id+"F4.imprint","IMPRINT",EDGE,{"derivedFrom":sQuery(id+"F4.wireOp",EDGE,"E66.MirrorC")}),-1.0]])]});
            var Q31;
            Q31=makeQuery(id+"F4.imprint","IMPRINT",FACE,{"disambiguationData":[TD([[makeQuery(id+"F4.imprint","IMPRINT",EDGE,{"derivedFrom":sQuery(id+"F4.wireOp",EDGE,"E73.MirrorC")}),-1.0]])]});
            var Q32;
            Q32=makeQuery(id+"F4.imprint","IMPRINT",FACE,{"disambiguationData":[TD([[makeQuery(id+"F4.imprint","IMPRINT",EDGE,{"derivedFrom":sQuery(id+"F4.wireOp",EDGE,"E107.MirrorC")}),-1.0]])]});
            var Q33;
            Q33=makeQuery(id+"F4.imprint","IMPRINT",FACE,{"disambiguationData":[TD([[makeQuery(id+"F4.imprint","IMPRINT",EDGE,{"derivedFrom":sQuery(id+"F4.wireOp",EDGE,"E90.MirrorC")}),-1.0]])]});
            var Q34;
            Q34=makeQuery(id+"F4.imprint","IMPRINT",FACE,{"disambiguationData":[TD([[makeQuery(id+"F4.imprint","IMPRINT",EDGE,{"derivedFrom":sQuery(id+"F4.wireOp",EDGE,"E74.MirrorC")}),-1.0]])]});
            var Q35;
            Q35=makeQuery(id+"F4.imprint","IMPRINT",FACE,{"disambiguationData":[TD([[makeQuery(id+"F4.imprint","IMPRINT",EDGE,{"derivedFrom":sQuery(id+"F4.wireOp",EDGE,"E58.MirrorC")}),-1.0]])]});
            var Q36;
            Q36=makeQuery(id+"F4.imprint","IMPRINT",FACE,{"disambiguationData":[TD([[makeQuery(id+"F4.imprint","IMPRINT",EDGE,{"derivedFrom":sQuery(id+"F4.wireOp",EDGE,"E114.MirrorC")}),-1.0]])]});
            var Q37;
            Q37=makeQuery(id+"F4.imprint","IMPRINT",FACE,{"disambiguationData":[TD([[makeQuery(id+"F4.imprint","IMPRINT",EDGE,{"derivedFrom":sQuery(id+"F4.wireOp",EDGE,"E59.MirrorC")}),-1.0]])]});
            var Q38;
            Q38=makeQuery(id+"F4.imprint","IMPRINT",FACE,{"disambiguationData":[TD([[makeQuery(id+"F4.imprint","IMPRINT",EDGE,{"derivedFrom":sQuery(id+"F4.wireOp",EDGE,"E98.MirrorC")}),-1.0]])]});
            var Q39;
            Q39=makeQuery(id+"F4.imprint","IMPRINT",FACE,{"disambiguationData":[TD([[makeQuery(id+"F4.imprint","IMPRINT",EDGE,{"derivedFrom":sQuery(id+"F4.wireOp",EDGE,"E108.MirrorC")}),-1.0]])]});
            var Q40;
            Q40=makeQuery(id+"F4.imprint","IMPRINT",FACE,{"disambiguationData":[TD([[makeQuery(id+"F4.imprint","IMPRINT",EDGE,{"derivedFrom":sQuery(id+"F4.wireOp",EDGE,"E81.MirrorC")}),-1.0]])]});
            var Q41;
            Q41=makeQuery(id+"F4.imprint","IMPRINT",FACE,{"disambiguationData":[TD([[makeQuery(id+"F4.imprint","IMPRINT",EDGE,{"derivedFrom":sQuery(id+"F4.wireOp",EDGE,"E92.MirrorC")}),-1.0]])]});
            var Q42;
            Q42=makeQuery(id+"F4.imprint","IMPRINT",FACE,{"disambiguationData":[TD([[makeQuery(id+"F4.imprint","IMPRINT",EDGE,{"derivedFrom":sQuery(id+"F4.wireOp",EDGE,"E65.MirrorC")}),-1.0]])]});
            var Q43;
            Q43=makeQuery(id+"F4.imprint","IMPRINT",FACE,{"disambiguationData":[TD([[makeQuery(id+"F4.imprint","IMPRINT",EDGE,{"derivedFrom":sQuery(id+"F4.wireOp",EDGE,"E75.MirrorC")}),-1.0]])]});
            var Q44;
            Q44=makeQuery(id+"F4.imprint","IMPRINT",FACE,{"disambiguationData":[TD([[makeQuery(id+"F4.imprint","IMPRINT",EDGE,{"derivedFrom":sQuery(id+"F4.wireOp",EDGE,"E49.MirrorC")}),-1.0]])]});
            var Q45;
            Q45=makeQuery(id+"F4.imprint","IMPRINT",FACE,{"disambiguationData":[TD([[makeQuery(id+"F4.imprint","IMPRINT",EDGE,{"derivedFrom":sQuery(id+"F4.wireOp",EDGE,"E60.MirrorC")}),-1.0]])]});
            var Q46;
            Q46=makeQuery(id+"F4.imprint","IMPRINT",FACE,{"disambiguationData":[TD([[makeQuery(id+"F4.imprint","IMPRINT",EDGE,{"derivedFrom":sQuery(id+"F4.wireOp",EDGE,"E109.MirrorC")}),-1.0]])]});
            var Q47;
            Q47=makeQuery(id+"F4.imprint","IMPRINT",FACE,{"disambiguationData":[TD([[makeQuery(id+"F4.imprint","IMPRINT",EDGE,{"derivedFrom":sQuery(id+"F4.wireOp",EDGE,"E93.MirrorC")}),-1.0]])]});
            var Q48;
            Q48=makeQuery(id+"F4.imprint","IMPRINT",FACE,{"disambiguationData":[TD([[makeQuery(id+"F4.imprint","IMPRINT",EDGE,{"derivedFrom":sQuery(id+"F4.wireOp",EDGE,"E76.MirrorC")}),-1.0]])]});
            var Q49;
            Q49=makeQuery(id+"F4.imprint","IMPRINT",FACE,{"disambiguationData":[TD([[makeQuery(id+"F4.imprint","IMPRINT",EDGE,{"derivedFrom":sQuery(id+"F4.wireOp",EDGE,"E79.MirrorC")}),-1.0]])]});
            var Q50;
            Q50=makeQuery(id+"F4.imprint","IMPRINT",FACE,{"disambiguationData":[TD([[makeQuery(id+"F4.imprint","IMPRINT",EDGE,{"derivedFrom":sQuery(id+"F4.wireOp",EDGE,"E63.MirrorC")}),-1.0]])]});
            var Q51;
            Q51=makeQuery(id+"F4.imprint","IMPRINT",FACE,{"disambiguationData":[TD([[makeQuery(id+"F4.imprint","IMPRINT",EDGE,{"derivedFrom":sQuery(id+"F4.wireOp",EDGE,"E47.MirrorC")}),-1.0]])]});
            var Q52;
            Q52=makeQuery(id+"F4.imprint","IMPRINT",FACE,{"disambiguationData":[TD([[makeQuery(id+"F4.imprint","IMPRINT",EDGE,{"derivedFrom":sQuery(id+"F4.wireOp",EDGE,"E112.MirrorC")}),-1.0]])]});
            var Q53;
            Q53=makeQuery(id+"F4.imprint","IMPRINT",FACE,{"disambiguationData":[TD([[makeQuery(id+"F4.imprint","IMPRINT",EDGE,{"derivedFrom":sQuery(id+"F4.wireOp",EDGE,"E96.MirrorC")}),-1.0]])]});
            var Q54;
            Q54=makeQuery(id+"F4.imprint","IMPRINT",FACE,{"disambiguationData":[TD([[makeQuery(id+"F4.imprint","IMPRINT",EDGE,{"derivedFrom":sQuery(id+"F4.wireOp",EDGE,"E61.MirrorC")}),-1.0]])]});
            var Q55;
            Q55=makeQuery(id+"F4.imprint","IMPRINT",FACE,{"disambiguationData":[TD([[makeQuery(id+"F4.imprint","IMPRINT",EDGE,{"derivedFrom":sQuery(id+"F4.wireOp",EDGE,"E45.MirrorC")}),-1.0]])]});
            var Q56;
            Q56=makeQuery(id+"F4.imprint","IMPRINT",FACE,{"disambiguationData":[TD([[makeQuery(id+"F4.imprint","IMPRINT",EDGE,{"derivedFrom":sQuery(id+"F4.wireOp",EDGE,"E110.MirrorC")}),-1.0]])]});
            var Q57;
            Q57=makeQuery(id+"F4.imprint","IMPRINT",FACE,{"disambiguationData":[TD([[makeQuery(id+"F4.imprint","IMPRINT",EDGE,{"derivedFrom":sQuery(id+"F4.wireOp",EDGE,"E94.MirrorC")}),-1.0]])]});
            var Q58;
            Q58=makeQuery(id+"F4.imprint","IMPRINT",FACE,{"disambiguationData":[TD([[makeQuery(id+"F4.imprint","IMPRINT",EDGE,{"derivedFrom":sQuery(id+"F4.wireOp",EDGE,"E77.MirrorC")}),-1.0]])]});
            var Q59;
            Q59=makeQuery(id+"F4.imprint","IMPRINT",FACE,{"disambiguationData":[TD([[makeQuery(id+"F4.imprint","IMPRINT",EDGE,{"derivedFrom":sQuery(id+"F4.wireOp",EDGE,"E80.MirrorC")}),-1.0]])]});
            var Q60;
            Q60=makeQuery(id+"F4.imprint","IMPRINT",FACE,{"disambiguationData":[TD([[makeQuery(id+"F4.imprint","IMPRINT",EDGE,{"derivedFrom":sQuery(id+"F4.wireOp",EDGE,"E64.MirrorC")}),-1.0]])]});
            var Q61;
            Q61=makeQuery(id+"F4.imprint","IMPRINT",FACE,{"disambiguationData":[TD([[makeQuery(id+"F4.imprint","IMPRINT",EDGE,{"derivedFrom":sQuery(id+"F4.wireOp",EDGE,"E48.MirrorC")}),-1.0]])]});
            var Q62;
            Q62=makeQuery(id+"F4.imprint","IMPRINT",FACE,{"disambiguationData":[TD([[makeQuery(id+"F4.imprint","IMPRINT",EDGE,{"derivedFrom":sQuery(id+"F4.wireOp",EDGE,"E113.MirrorC")}),-1.0]])]});
            var Q63;
            Q63=makeQuery(id+"F4.imprint","IMPRINT",FACE,{"disambiguationData":[TD([[makeQuery(id+"F4.imprint","IMPRINT",EDGE,{"derivedFrom":sQuery(id+"F4.wireOp",EDGE,"E97.MirrorC")}),-1.0]])]});
            var Q64;
            Q64=makeQuery(id+"F4.imprint","IMPRINT",FACE,{"disambiguationData":[TD([[makeQuery(id+"F4.imprint","IMPRINT",EDGE,{"derivedFrom":sQuery(id+"F4.wireOp",EDGE,"E62.MirrorC")}),-1.0]])]});
            var Q65;
            Q65=makeQuery(id+"F4.imprint","IMPRINT",FACE,{"disambiguationData":[TD([[makeQuery(id+"F4.imprint","IMPRINT",EDGE,{"derivedFrom":sQuery(id+"F4.wireOp",EDGE,"E46.MirrorC")}),-1.0]])]});
            var Q66;
            Q66=makeQuery(id+"F4.imprint","IMPRINT",FACE,{"disambiguationData":[TD([[makeQuery(id+"F4.imprint","IMPRINT",EDGE,{"derivedFrom":sQuery(id+"F4.wireOp",EDGE,"E111.MirrorC")}),-1.0]])]});
            var Q67;
            Q67=makeQuery(id+"F4.imprint","IMPRINT",FACE,{"disambiguationData":[TD([[makeQuery(id+"F4.imprint","IMPRINT",EDGE,{"derivedFrom":sQuery(id+"F4.wireOp",EDGE,"E95.MirrorC")}),-1.0]])]});
            var Q68;
            Q68=makeQuery(id+"F4.imprint","IMPRINT",FACE,{"disambiguationData":[TD([[makeQuery(id+"F4.imprint","IMPRINT",EDGE,{"derivedFrom":sQuery(id+"F4.wireOp",EDGE,"E78.MirrorC")}),-1.0]])]});
            var Q69;
            Q69=makeQuery(id+"F4.imprint","IMPRINT",FACE,{"disambiguationData":[TD([[makeQuery(id+"F4.imprint","IMPRINT",EDGE,{"derivedFrom":sQuery(id+"F4.wireOp",EDGE,"E43.MirrorC")}),-1.0]])]});
            var Q70;
            Q70=makeQuery(id+"F4.imprint","IMPRINT",FACE,{"disambiguationData":[TD([[makeQuery(id+"F4.imprint","IMPRINT",EDGE,{"derivedFrom":sQuery(id+"F4.wireOp",EDGE,"E44.MirrorC")}),-1.0]])]});
            var Q71;
            Q71=makeQuery(id+"F4.imprint","IMPRINT",FACE,{"disambiguationData":[TD([[makeQuery(id+"F4.imprint","IMPRINT",EDGE,{"derivedFrom":sQuery(id+"F4.wireOp",EDGE,"E42.MirrorC")}),-1.0]])]});
            var Q72;
            Q72=makeQuery(id+"F4.imprint","IMPRINT",FACE,{"disambiguationData":[TD([[makeQuery(id+"F4.imprint","IMPRINT",EDGE,{"derivedFrom":sQuery(id+"F4.wireOp",EDGE,"E41.3.3.0")}),1.0]])]});
            var Q73;
            Q73=makeQuery(id+"F4.imprint","IMPRINT",FACE,{"disambiguationData":[TD([[makeQuery(id+"F4.imprint","IMPRINT",EDGE,{"derivedFrom":sQuery(id+"F4.wireOp",EDGE,"E41.4.7.0")}),1.0]])]});
            var Q74;
            Q74=makeQuery(id+"F4.imprint","IMPRINT",FACE,{"disambiguationData":[TD([[makeQuery(id+"F4.imprint","IMPRINT",EDGE,{"derivedFrom":sQuery(id+"F4.wireOp",EDGE,"E41.5.11.0")}),1.0]])]});
            var Q75;
            Q75=makeQuery(id+"F4.imprint","IMPRINT",FACE,{"disambiguationData":[TD([[makeQuery(id+"F4.imprint","IMPRINT",EDGE,{"derivedFrom":sQuery(id+"F4.wireOp",EDGE,"E41.5.8.0")}),1.0]])]});
            var Q76;
            Q76=makeQuery(id+"F4.imprint","IMPRINT",FACE,{"disambiguationData":[TD([[makeQuery(id+"F4.imprint","IMPRINT",EDGE,{"derivedFrom":sQuery(id+"F4.wireOp",EDGE,"E41.1.8.0")}),1.0]])]});
            var Q77;
            Q77=makeQuery(id+"F4.imprint","IMPRINT",FACE,{"disambiguationData":[TD([[makeQuery(id+"F4.imprint","IMPRINT",EDGE,{"derivedFrom":sQuery(id+"F4.wireOp",EDGE,"E41.3.2.0")}),1.0]])]});
            var Q78;
            Q78=makeQuery(id+"F4.imprint","IMPRINT",FACE,{"disambiguationData":[TD([[makeQuery(id+"F4.imprint","IMPRINT",EDGE,{"derivedFrom":sQuery(id+"F4.wireOp",EDGE,"E41.3.0.0")}),1.0]])]});
            var Q79;
            Q79=makeQuery(id+"F4.imprint","IMPRINT",FACE,{"disambiguationData":[TD([[makeQuery(id+"F4.imprint","IMPRINT",EDGE,{"derivedFrom":sQuery(id+"F4.wireOp",EDGE,"E41.4.6.0")}),1.0]])]});
            var Q80;
            Q80=makeQuery(id+"F4.imprint","IMPRINT",FACE,{"disambiguationData":[TD([[makeQuery(id+"F4.imprint","IMPRINT",EDGE,{"derivedFrom":sQuery(id+"F4.wireOp",EDGE,"E41.4.4.0")}),1.0]])]});
            var Q81;
            Q81=makeQuery(id+"F4.imprint","IMPRINT",FACE,{"disambiguationData":[TD([[makeQuery(id+"F4.imprint","IMPRINT",EDGE,{"derivedFrom":sQuery(id+"F4.wireOp",EDGE,"E41.5.10.0")}),1.0]])]});
            var Q82;
            Q82=makeQuery(id+"F4.imprint","IMPRINT",FACE,{"disambiguationData":[TD([[makeQuery(id+"F4.imprint","IMPRINT",EDGE,{"derivedFrom":sQuery(id+"F4.wireOp",EDGE,"E41.1.10.0")}),1.0]])]});
            var Q83;
            Q83=makeQuery(id+"F4.imprint","IMPRINT",FACE,{"disambiguationData":[TD([[makeQuery(id+"F4.imprint","IMPRINT",EDGE,{"derivedFrom":sQuery(id+"F4.wireOp",EDGE,"E41.5.7.0")}),1.0]])]});
            var Q84;
            Q84=makeQuery(id+"F4.imprint","IMPRINT",FACE,{"disambiguationData":[TD([[makeQuery(id+"F4.imprint","IMPRINT",EDGE,{"derivedFrom":sQuery(id+"F4.wireOp",EDGE,"E41.1.7.0")}),1.0]])]});
            var Q85;
            Q85=makeQuery(id+"F4.imprint","IMPRINT",FACE,{"disambiguationData":[TD([[makeQuery(id+"F4.imprint","IMPRINT",EDGE,{"derivedFrom":sQuery(id+"F4.wireOp",EDGE,"E41.2.11.0")}),1.0]])]});
            var Q86;
            Q86=makeQuery(id+"F4.imprint","IMPRINT",FACE,{"disambiguationData":[TD([[makeQuery(id+"F4.imprint","IMPRINT",EDGE,{"derivedFrom":sQuery(id+"F4.wireOp",EDGE,"E41.4.3.0")}),1.0]])]});
            var Q87;
            Q87=makeQuery(id+"F4.imprint","IMPRINT",FACE,{"disambiguationData":[TD([[makeQuery(id+"F4.imprint","IMPRINT",EDGE,{"derivedFrom":sQuery(id+"F4.wireOp",EDGE,"E41.5.6.0")}),1.0]])]});
            var Q88;
            Q88=makeQuery(id+"F4.imprint","IMPRINT",FACE,{"disambiguationData":[TD([[makeQuery(id+"F4.imprint","IMPRINT",EDGE,{"derivedFrom":sQuery(id+"F4.wireOp",EDGE,"E41.5.9.0")}),1.0]])]});
            var Q89;
            Q89=makeQuery(id+"F4.imprint","IMPRINT",FACE,{"disambiguationData":[TD([[makeQuery(id+"F4.imprint","IMPRINT",EDGE,{"derivedFrom":sQuery(id+"F4.wireOp",EDGE,"E41.1.6.0")}),1.0]])]});
            var Q90;
            Q90=makeQuery(id+"F4.imprint","IMPRINT",FACE,{"disambiguationData":[TD([[makeQuery(id+"F4.imprint","IMPRINT",EDGE,{"derivedFrom":sQuery(id+"F4.wireOp",EDGE,"E41.2.10.0")}),1.0]])]});
            var Q91;
            Q91=makeQuery(id+"F4.imprint","IMPRINT",FACE,{"disambiguationData":[TD([[makeQuery(id+"F4.imprint","IMPRINT",EDGE,{"derivedFrom":sQuery(id+"F4.wireOp",EDGE,"E41.4.2.0")}),1.0]])]});
            var Q92;
            Q92=makeQuery(id+"F4.imprint","IMPRINT",FACE,{"disambiguationData":[TD([[makeQuery(id+"F4.imprint","IMPRINT",EDGE,{"derivedFrom":sQuery(id+"F4.wireOp",EDGE,"E41.5.5.0")}),1.0]])]});
            var Q93;
            Q93=makeQuery(id+"F4.imprint","IMPRINT",FACE,{"disambiguationData":[TD([[makeQuery(id+"F4.imprint","IMPRINT",EDGE,{"derivedFrom":sQuery(id+"F4.wireOp",EDGE,"E41.1.5.0")}),1.0]])]});
            var Q94;
            Q94=makeQuery(id+"F4.imprint","IMPRINT",FACE,{"disambiguationData":[TD([[makeQuery(id+"F4.imprint","IMPRINT",EDGE,{"derivedFrom":sQuery(id+"F4.wireOp",EDGE,"E41.2.9.0")}),1.0]])]});
            var Q95;
            Q95=makeQuery(id+"F4.imprint","IMPRINT",FACE,{"disambiguationData":[TD([[makeQuery(id+"F4.imprint","IMPRINT",EDGE,{"derivedFrom":sQuery(id+"F4.wireOp",EDGE,"E41.4.1.0")}),1.0]])]});
            var Q96;
            Q96=makeQuery(id+"F4.imprint","IMPRINT",FACE,{"disambiguationData":[TD([[makeQuery(id+"F4.imprint","IMPRINT",EDGE,{"derivedFrom":sQuery(id+"F4.wireOp",EDGE,"E41.5.4.0")}),1.0]])]});
            var Q97;
            Q97=makeQuery(id+"F4.imprint","IMPRINT",FACE,{"disambiguationData":[TD([[makeQuery(id+"F4.imprint","IMPRINT",EDGE,{"derivedFrom":sQuery(id+"F4.wireOp",EDGE,"E41.1.9.0")}),1.0]])]});
            var Q98;
            Q98=makeQuery(id+"F4.imprint","IMPRINT",FACE,{"disambiguationData":[TD([[makeQuery(id+"F4.imprint","IMPRINT",EDGE,{"derivedFrom":sQuery(id+"F4.wireOp",EDGE,"E41.1.4.0")}),1.0]])]});
            var Q99;
            Q99=makeQuery(id+"F4.imprint","IMPRINT",FACE,{"disambiguationData":[TD([[makeQuery(id+"F4.imprint","IMPRINT",EDGE,{"derivedFrom":sQuery(id+"F4.wireOp",EDGE,"E41.2.8.0")}),1.0]])]});
            var Q100;
            Q100=makeQuery(id+"F4.imprint","IMPRINT",FACE,{"disambiguationData":[TD([[makeQuery(id+"F4.imprint","IMPRINT",EDGE,{"derivedFrom":sQuery(id+"F4.wireOp",EDGE,"E41.3.1.0")}),1.0]])]});
            var Q101;
            Q101=makeQuery(id+"F4.imprint","IMPRINT",FACE,{"disambiguationData":[TD([[makeQuery(id+"F4.imprint","IMPRINT",EDGE,{"derivedFrom":sQuery(id+"F4.wireOp",EDGE,"E41.4.5.0")}),1.0]])]});
            var Q102;
            Q102=makeQuery(id+"F4.imprint","IMPRINT",FACE,{"disambiguationData":[TD([[makeQuery(id+"F4.imprint","IMPRINT",EDGE,{"derivedFrom":sQuery(id+"F4.wireOp",EDGE,"E41.4.0.0")}),1.0]])]});
            var Q103;
            Q103=makeQuery(id+"F4.imprint","IMPRINT",FACE,{"disambiguationData":[TD([[makeQuery(id+"F4.imprint","IMPRINT",EDGE,{"derivedFrom":sQuery(id+"F4.wireOp",EDGE,"E41.1.11.0")}),1.0]])]});
            var Q104;
            Q104=makeQuery(id+"F4.imprint","IMPRINT",FACE,{"disambiguationData":[TD([[makeQuery(id+"F4.imprint","IMPRINT",EDGE,{"derivedFrom":sQuery(id+"F4.wireOp",EDGE,"E41.2.0.0")}),1.0]])]});
            var Q105;
            Q105=makeQuery(id+"F4.imprint","IMPRINT",FACE,{"disambiguationData":[TD([[makeQuery(id+"F4.imprint","IMPRINT",EDGE,{"derivedFrom":sQuery(id+"F4.wireOp",EDGE,"E41.4.8.0")}),1.0]])]});
            var Q106;
            Q106=makeQuery(id+"F4.imprint","IMPRINT",FACE,{"disambiguationData":[TD([[makeQuery(id+"F4.imprint","IMPRINT",EDGE,{"derivedFrom":sQuery(id+"F4.wireOp",EDGE,"E41.3.4.0")}),1.0]])]});
            var Q107;
            Q107=makeQuery(id+"F4.imprint","IMPRINT",FACE,{"disambiguationData":[TD([[makeQuery(id+"F4.imprint","IMPRINT",EDGE,{"derivedFrom":sQuery(id+"F4.wireOp",EDGE,"E41.2.1.0")}),1.0]])]});
            var Q108;
            Q108=makeQuery(id+"F4.imprint","IMPRINT",FACE,{"disambiguationData":[TD([[makeQuery(id+"F4.imprint","IMPRINT",EDGE,{"derivedFrom":sQuery(id+"F4.wireOp",EDGE,"E41.5.3.0")}),1.0]])]});
            var Q109;
            Q109=makeQuery(id+"F4.imprint","IMPRINT",FACE,{"disambiguationData":[TD([[makeQuery(id+"F4.imprint","IMPRINT",EDGE,{"derivedFrom":sQuery(id+"F4.wireOp",EDGE,"E41.3.11.0")}),1.0]])]});
            var Q110;
            Q110=makeQuery(id+"F4.imprint","IMPRINT",FACE,{"disambiguationData":[TD([[makeQuery(id+"F4.imprint","IMPRINT",EDGE,{"derivedFrom":sQuery(id+"F4.wireOp",EDGE,"E41.4.9.0")}),1.0]])]});
            var Q111;
            Q111=makeQuery(id+"F4.imprint","IMPRINT",FACE,{"disambiguationData":[TD([[makeQuery(id+"F4.imprint","IMPRINT",EDGE,{"derivedFrom":sQuery(id+"F4.wireOp",EDGE,"E41.2.7.0")}),1.0]])]});
            var Q112;
            Q112=makeQuery(id+"F4.imprint","IMPRINT",FACE,{"disambiguationData":[TD([[makeQuery(id+"F4.imprint","IMPRINT",EDGE,{"derivedFrom":sQuery(id+"F4.wireOp",EDGE,"E41.3.5.0")}),1.0]])]});
            var Q113;
            Q113=makeQuery(id+"F4.imprint","IMPRINT",FACE,{"disambiguationData":[TD([[makeQuery(id+"F4.imprint","IMPRINT",EDGE,{"derivedFrom":sQuery(id+"F4.wireOp",EDGE,"E41.2.2.0")}),1.0]])]});
            var Q114;
            Q114=makeQuery(id+"F4.imprint","IMPRINT",FACE,{"disambiguationData":[TD([[makeQuery(id+"F4.imprint","IMPRINT",EDGE,{"derivedFrom":sQuery(id+"F4.wireOp",EDGE,"E41.4.10.0")}),1.0]])]});
            var Q115;
            Q115=makeQuery(id+"F4.imprint","IMPRINT",FACE,{"disambiguationData":[TD([[makeQuery(id+"F4.imprint","IMPRINT",EDGE,{"derivedFrom":sQuery(id+"F4.wireOp",EDGE,"E41.3.6.0")}),1.0]])]});
            var Q116;
            Q116=makeQuery(id+"F4.imprint","IMPRINT",FACE,{"disambiguationData":[TD([[makeQuery(id+"F4.imprint","IMPRINT",EDGE,{"derivedFrom":sQuery(id+"F4.wireOp",EDGE,"E41.3.9.0")}),1.0]])]});
            var Q117;
            Q117=makeQuery(id+"F4.imprint","IMPRINT",FACE,{"disambiguationData":[TD([[makeQuery(id+"F4.imprint","IMPRINT",EDGE,{"derivedFrom":sQuery(id+"F4.wireOp",EDGE,"E41.2.5.0")}),1.0]])]});
            var Q118;
            Q118=makeQuery(id+"F4.imprint","IMPRINT",FACE,{"disambiguationData":[TD([[makeQuery(id+"F4.imprint","IMPRINT",EDGE,{"derivedFrom":sQuery(id+"F4.wireOp",EDGE,"E41.5.1.0")}),1.0]])]});
            var Q119;
            Q119=makeQuery(id+"F4.imprint","IMPRINT",FACE,{"disambiguationData":[TD([[makeQuery(id+"F4.imprint","IMPRINT",EDGE,{"derivedFrom":sQuery(id+"F4.wireOp",EDGE,"E41.1.3.0")}),1.0]])]});
            var Q120;
            Q120=makeQuery(id+"F4.imprint","IMPRINT",FACE,{"disambiguationData":[TD([[makeQuery(id+"F4.imprint","IMPRINT",EDGE,{"derivedFrom":sQuery(id+"F4.wireOp",EDGE,"E41.1.1.0")}),1.0]])]});
            var Q121;
            Q121=makeQuery(id+"F4.imprint","IMPRINT",FACE,{"disambiguationData":[TD([[makeQuery(id+"F4.imprint","IMPRINT",EDGE,{"derivedFrom":sQuery(id+"F4.wireOp",EDGE,"E41.1.2.0")}),1.0]])]});
            var Q122;
            Q122=makeQuery(id+"F4.imprint","IMPRINT",FACE,{"disambiguationData":[TD([[makeQuery(id+"F4.imprint","IMPRINT",EDGE,{"derivedFrom":sQuery(id+"F4.wireOp",EDGE,"E41.0.2.0")}),1.0]])]});
            var Q123;
            Q123=makeQuery(id+"F4.imprint","IMPRINT",FACE,{"disambiguationData":[TD([[makeQuery(id+"F4.imprint","IMPRINT",EDGE,{"derivedFrom":sQuery(id+"F4.wireOp",EDGE,"E41.2.3.0")}),1.0]])]});
            var Q124;
            Q124=makeQuery(id+"F4.imprint","IMPRINT",FACE,{"disambiguationData":[TD([[makeQuery(id+"F4.imprint","IMPRINT",EDGE,{"derivedFrom":sQuery(id+"F4.wireOp",EDGE,"E41.0.3.0")}),1.0]])]});
            var Q125;
            Q125=makeQuery(id+"F4.imprint","IMPRINT",FACE,{"disambiguationData":[TD([[makeQuery(id+"F4.imprint","IMPRINT",EDGE,{"derivedFrom":sQuery(id+"F4.wireOp",EDGE,"E41.0.4.0")}),1.0]])]});
            var Q126;
            Q126=makeQuery(id+"F4.imprint","IMPRINT",FACE,{"disambiguationData":[TD([[makeQuery(id+"F4.imprint","IMPRINT",EDGE,{"derivedFrom":sQuery(id+"F4.wireOp",EDGE,"E41.4.11.0")}),1.0]])]});
            var Q127;
            Q127=makeQuery(id+"F4.imprint","IMPRINT",FACE,{"disambiguationData":[TD([[makeQuery(id+"F4.imprint","IMPRINT",EDGE,{"derivedFrom":sQuery(id+"F4.wireOp",EDGE,"E41.3.7.0")}),1.0]])]});
            var Q128;
            Q128=makeQuery(id+"F4.imprint","IMPRINT",FACE,{"disambiguationData":[TD([[makeQuery(id+"F4.imprint","IMPRINT",EDGE,{"derivedFrom":sQuery(id+"F4.wireOp",EDGE,"E41.0.5.0")}),1.0]])]});
            var Q129;
            Q129=makeQuery(id+"F4.imprint","IMPRINT",FACE,{"disambiguationData":[TD([[makeQuery(id+"F4.imprint","IMPRINT",EDGE,{"derivedFrom":sQuery(id+"F4.wireOp",EDGE,"E41.0.6.0")}),1.0]])]});
            var Q130;
            Q130=makeQuery(id+"F4.imprint","IMPRINT",FACE,{"disambiguationData":[TD([[makeQuery(id+"F4.imprint","IMPRINT",EDGE,{"derivedFrom":sQuery(id+"F4.wireOp",EDGE,"E41.0.7.0")}),1.0]])]});
            var Q131;
            Q131=makeQuery(id+"F4.imprint","IMPRINT",FACE,{"disambiguationData":[TD([[makeQuery(id+"F4.imprint","IMPRINT",EDGE,{"derivedFrom":sQuery(id+"F4.wireOp",EDGE,"E41.0.8.0")}),1.0]])]});
            var Q132;
            Q132=makeQuery(id+"F4.imprint","IMPRINT",FACE,{"disambiguationData":[TD([[makeQuery(id+"F4.imprint","IMPRINT",EDGE,{"derivedFrom":sQuery(id+"F4.wireOp",EDGE,"E41.0.9.0")}),1.0]])]});
            var Q133;
            Q133=makeQuery(id+"F4.imprint","IMPRINT",FACE,{"disambiguationData":[TD([[makeQuery(id+"F4.imprint","IMPRINT",EDGE,{"derivedFrom":sQuery(id+"F4.wireOp",EDGE,"E41.3.10.0")}),1.0]])]});
            var Q134;
            Q134=makeQuery(id+"F4.imprint","IMPRINT",FACE,{"disambiguationData":[TD([[makeQuery(id+"F4.imprint","IMPRINT",EDGE,{"derivedFrom":sQuery(id+"F4.wireOp",EDGE,"E41.2.6.0")}),1.0]])]});
            var Q135;
            Q135=makeQuery(id+"F4.imprint","IMPRINT",FACE,{"disambiguationData":[TD([[makeQuery(id+"F4.imprint","IMPRINT",EDGE,{"derivedFrom":sQuery(id+"F4.wireOp",EDGE,"E41.0.10.0")}),1.0]])]});
            var Q136;
            Q136=makeQuery(id+"F4.imprint","IMPRINT",FACE,{"disambiguationData":[TD([[makeQuery(id+"F4.imprint","IMPRINT",EDGE,{"derivedFrom":sQuery(id+"F4.wireOp",EDGE,"E41.0.11.0")}),1.0]])]});
            var Q137;
            Q137=makeQuery(id+"F4.imprint","IMPRINT",FACE,{"disambiguationData":[TD([[makeQuery(id+"F4.imprint","IMPRINT",EDGE,{"derivedFrom":sQuery(id+"F4.wireOp",EDGE,"E41.5.2.0")}),1.0]])]});
            var Q138;
            Q138=makeQuery(id+"F4.imprint","IMPRINT",FACE,{"disambiguationData":[TD([[makeQuery(id+"F4.imprint","IMPRINT",EDGE,{"derivedFrom":sQuery(id+"F4.wireOp",EDGE,"E41.2.4.0")}),1.0]])]});
            var Q139;
            Q139=makeQuery(id+"F4.imprint","IMPRINT",FACE,{"disambiguationData":[TD([[makeQuery(id+"F4.imprint","IMPRINT",EDGE,{"derivedFrom":sQuery(id+"F4.wireOp",EDGE,"E41.5.0.0")}),1.0]])]});
            var Q140;
            Q140=makeQuery(id+"F4.imprint","IMPRINT",FACE,{"disambiguationData":[TD([[makeQuery(id+"F4.imprint","IMPRINT",EDGE,{"derivedFrom":sQuery(id+"F4.wireOp",EDGE,"E41.3.8.0")}),1.0]])]});
            var Q141;
            Q141=makeQuery(id+"F4.imprint","IMPRINT",FACE,{"disambiguationData":[TD([[makeQuery(id+"F4.imprint","IMPRINT",EDGE,{"derivedFrom":sQuery(id+"F4.wireOp",EDGE,"E41.0.1.0")}),1.0]])]});
            var Q142;
            Q142=makeQuery(id+"F4.imprint","IMPRINT",FACE,{"disambiguationData":[TD([[makeQuery(id+"F4.imprint","IMPRINT",EDGE,{"derivedFrom":sQuery(id+"F4.wireOp",EDGE,"E41.1.0.0")}),1.0]])]});
            var Q143;
            Q143=makeQuery(id+"F4.imprint","IMPRINT",FACE,{"disambiguationData":[TD([[makeQuery(id+"F4.imprint","IMPRINT",EDGE,{"derivedFrom":sQuery(id+"F4.wireOp",EDGE,"E40")}),1.0]])]});
            extrude(context, id + "F5", {"entities" : qUnion([Q0, Q1, Q2, Q3, Q4, Q5, Q6, Q7, Q8, Q9, Q10, Q11, Q12, Q13, Q14, Q15, Q16, Q17, Q18, Q19, Q20, Q21, Q22, Q23, Q24, Q25, Q26, Q27, Q28, Q29, Q30, Q31, Q32, Q33, Q34, Q35, Q36, Q37, Q38, Q39, Q40, Q41, Q42, Q43, Q44, Q45, Q46, Q47, Q48, Q49, Q50, Q51, Q52, Q53, Q54, Q55, Q56, Q57, Q58, Q59, Q60, Q61, Q62, Q63, Q64, Q65, Q66, Q67, Q68, Q69, Q70, Q71, Q72, Q73, Q74, Q75, Q76, Q77, Q78, Q79, Q80, Q81, Q82, Q83, Q84, Q85, Q86, Q87, Q88, Q89, Q90, Q91, Q92, Q93, Q94, Q95, Q96, Q97, Q98, Q99, Q100, Q101, Q102, Q103, Q104, Q105, Q106, Q107, Q108, Q109, Q110, Q111, Q112, Q113, Q114, Q115, Q116, Q117, Q118, Q119, Q120, Q121, Q122, Q123, Q124, Q125, Q126, Q127, Q128, Q129, Q130, Q131, Q132, Q133, Q134, Q135, Q136, Q137, Q138, Q139, Q140, Q141, Q142, Q143]), "operationType" : NewBodyOperationType.REMOVE, "endBound" : BoundingType.UP_TO_NEXT, "oppositeDirection" : true, "depth" : 25 * mm});
        }
    });
